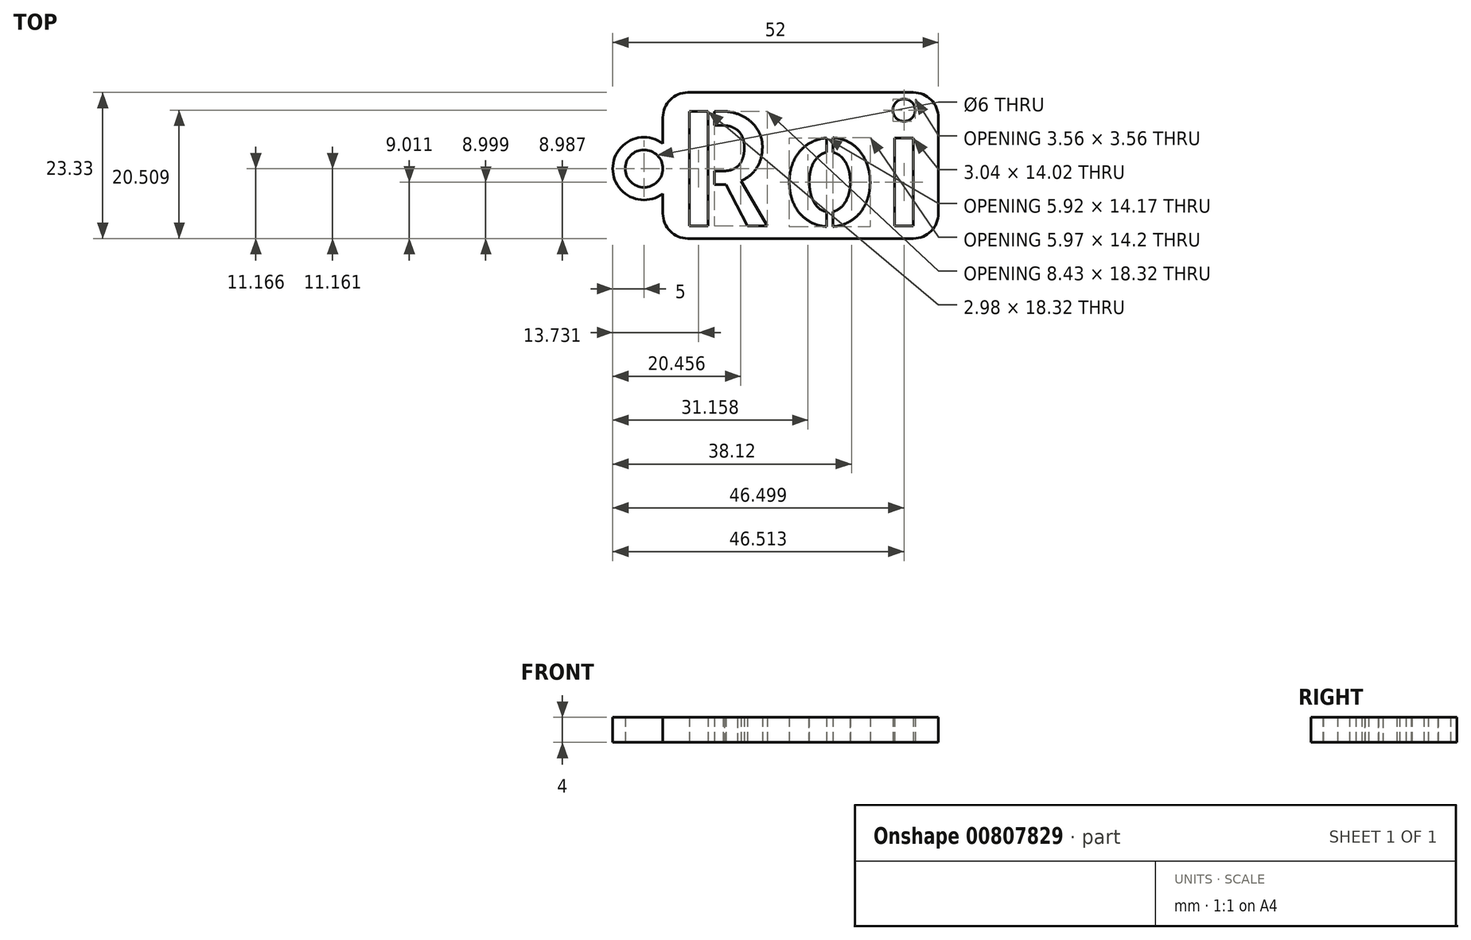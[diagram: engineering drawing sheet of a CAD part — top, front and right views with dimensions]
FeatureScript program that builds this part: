
annotation { "Feature Type Name" : "Feature", "Feature Type Description" : "" }
export const myFeature = defineFeature(function(context is Context, id is Id, definition is map)
    precondition{}
    {
        {
            var Q0;
            Q0=qCreatedBy(makeId("Top.planeOp"),FACE);
            var sketch = newSketch(context, id + "F0", { "sketchPlane" : qUnion([Q0])});
            skText(sketch, "E0", { "text": "Roi", "fontName": "AllertaStencil-Regular.ttf"});
            skLineSegment(sketch, "E1.bottom", {"start": v(-2, -2) * mm, "end": v(42, -2) * mm});
            skLineSegment(sketch, "E1.top", {"start": v(-2, 21.33) * mm, "end": v(42, 21.33) * mm});
            skLineSegment(sketch, "E1.left", {"start": v(-2, -2) * mm, "end": v(-2, 5.17) * mm});
            skLineSegment(sketch, "E1.right", {"start": v(42, -2) * mm, "end": v(42, 21.33) * mm});
            skArc(sketch, "E2", {"start": v(-2, 13.17) * mm, "mid": v(-10, 9.17) * mm, "end": v(-2, 5.17) * mm});
            skPoint(sketch, "E2.centerSnap0", {"position": v(0, 9.17) * mm});
            skLineSegment(sketch, "E3.trimOffspring", {"start": v(-2, 13.17) * mm, "end": v(-2, 21.33) * mm});
            skCircle(sketch, "E4", {"center": v(-5, 9.17) * mm, "radius": 3 * mm});
            const initialGuessF0  = {"E0": [0, 0, 1, 0, 0.01833]};
            skSetInitialGuess(sketch, initialGuessF0);
            skSolve(sketch);
        }
        {
            var Q0;
            Q0=makeQuery(id+"F0.imprint","IMPRINT",FACE,{"disambiguationData":[TD([[makeQuery(id+"F0.imprint","IMPRINT",EDGE,{"derivedFrom":sQuery(id+"F0.wireOp",EDGE,"E0.sketch_text.stroke-0")}),1.0]])]});
            extrude(context, id + "F1", {"entities" : qUnion([Q0]), "depth" : 4 * mm, "offsetDistance" : 25 * mm});
        }
        {
            var Q0;
            Q0=makeQuery(id+"F1.opExtrude","SWEPT_EDGE",EDGE,{"disambiguationData":[OSD([sQuery(id+"F0.wireOp",EDGE,"E1.bottom"),sQuery(id+"F0.wireOp",EDGE,"E1.right")])]});
            var Q1;
            Q1=makeQuery(id+"F1.opExtrude","SWEPT_EDGE",EDGE,{"disambiguationData":[OSD([sQuery(id+"F0.wireOp",EDGE,"E1.top"),sQuery(id+"F0.wireOp",EDGE,"E1.right")])]});
            var Q2;
            Q2=makeQuery(id+"F1.opExtrude","SWEPT_EDGE",EDGE,{"disambiguationData":[OSD([sQuery(id+"F0.wireOp",EDGE,"E1.bottom"),sQuery(id+"F0.wireOp",EDGE,"E1.left")])]});
            var Q3;
            Q3=makeQuery(id+"F1.opExtrude","SWEPT_EDGE",EDGE,{"disambiguationData":[OSD([sQuery(id+"F0.wireOp",EDGE,"E1.top"),sQuery(id+"F0.wireOp",EDGE,"E3.trimOffspring")])]});
            fillet(context, id + "F2", {"entities" : qUnion([Q0, Q1, Q2, Q3]), "radius" : 4 * mm, "tangentPropagation" : true, "allowEdgeOverflow" : false});
        }
    });
